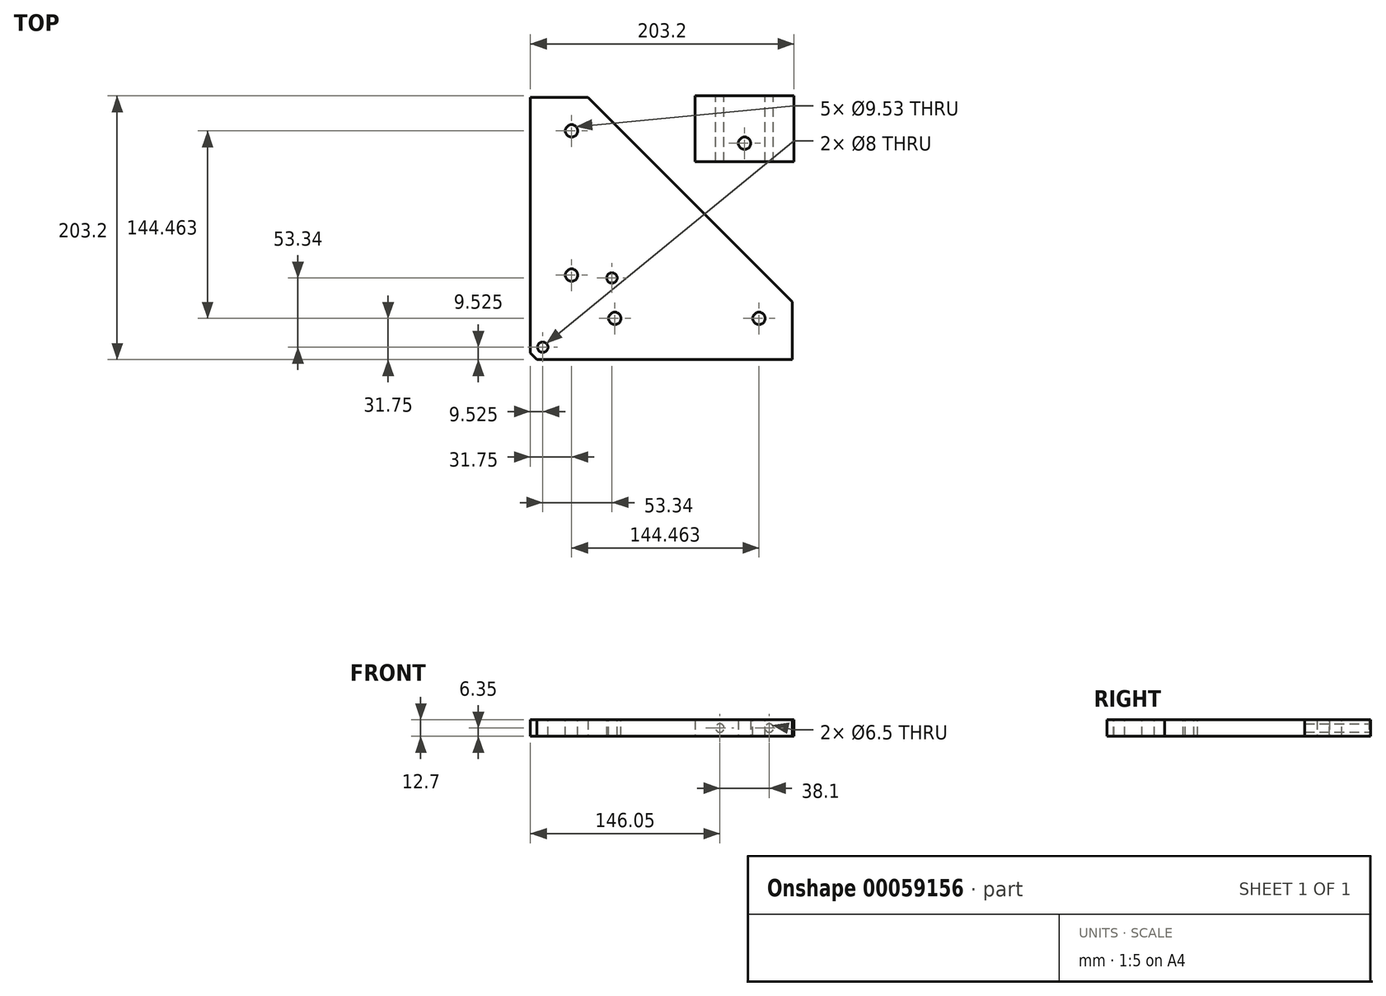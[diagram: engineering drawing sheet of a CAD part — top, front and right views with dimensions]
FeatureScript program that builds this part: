
annotation { "Feature Type Name" : "Feature", "Feature Type Description" : "" }
export const myFeature = defineFeature(function(context is Context, id is Id, definition is map)
    precondition{}
    {
        {
            var Q0;
            Q0=qCreatedBy(makeId("Top.planeOp"),FACE);
            var sketch = newSketch(context, id + "F0", { "sketchPlane" : qUnion([Q0])});
            skLineSegment(sketch, "E0", {"start": v(0, 0) * mm, "end": v(201.93, 0) * mm});
            skLineSegment(sketch, "E1", {"start": v(201.93, 0) * mm, "end": v(201.93, 44.45) * mm});
            skLineSegment(sketch, "E2", {"start": v(201.93, 44.45) * mm, "end": v(44.45, 201.93) * mm});
            skLineSegment(sketch, "E3", {"start": v(44.45, 201.93) * mm, "end": v(0, 201.93) * mm});
            skLineSegment(sketch, "E4", {"start": v(0, 201.93) * mm, "end": v(0, 0) * mm});
            skSolve(sketch);
        }
        {
            var Q0;
            Q0 = qSketchRegion(id + "F0", true);
            extrude(context, id + "F1", {"entities" : qUnion([Q0]), "depth" : 12.7 * mm});
        }
        {
            var Q0;
            Q0=makeQuery(id+"F1.opExtrude","CAP_FACE",FACE,{"disambiguationData":[OSD([sQuery(id+"F0.wireOp",EDGE,"E0"),sQuery(id+"F0.wireOp",EDGE,"E1"),sQuery(id+"F0.wireOp",EDGE,"E2"),sQuery(id+"F0.wireOp",EDGE,"E3"),sQuery(id+"F0.wireOp",EDGE,"E4")])],"isStart":false});
            var sketch = newSketch(context, id + "F2", { "sketchPlane" : qUnion([Q0])});
            skLineSegment(sketch, "E5", {"start": v(201.93, 31.75) * mm, "end": v(44.45, 31.75) * mm, "construction": true});
            skPoint(sketch, "E6", {"position": v(44.45, 31.75) * mm});
            skPoint(sketch, "E7.1.0.0", {"position": v(63.5, 31.75) * mm});
            skPoint(sketch, "E7.2.0.0", {"position": v(82.55, 31.75) * mm});
            skPoint(sketch, "E7.3.0.0", {"position": v(101.6, 31.75) * mm});
            skPoint(sketch, "E7.4.0.0", {"position": v(120.65, 31.75) * mm});
            skPoint(sketch, "E7.5.0.0", {"position": v(139.7, 31.75) * mm});
            skPoint(sketch, "E7.6.0.0", {"position": v(158.75, 31.75) * mm});
            skPoint(sketch, "E7.7.0.0", {"position": v(177.8, 31.75) * mm});
            skLineSegment(sketch, "E7.direction1", {"start": v(44.45, 31.75) * mm, "end": v(63.5, 31.75) * mm, "construction": true});
            skCircle(sketch, "E8", {"center": v(65.09, 31.75) * mm, "radius": 4.76 * mm});
            skCircle(sketch, "E9", {"center": v(176.21, 31.75) * mm, "radius": 4.76 * mm});
            skLineSegment(sketch, "E10", {"start": v(0, 0) * mm, "end": v(171.64, 171.64) * mm, "construction": true});
            skCircle(sketch, "E11.MirrorC", {"center": v(31.75, 176.21) * mm, "radius": 4.76 * mm});
            skCircle(sketch, "E12.MirrorC", {"center": v(31.75, 65.09) * mm, "radius": 4.76 * mm});
            skCircle(sketch, "E13", {"center": v(9.52, 9.53) * mm, "radius": 4 * mm});
            skCircle(sketch, "E14", {"center": v(62.87, 62.87) * mm, "radius": 4 * mm});
            skSolve(sketch);
        }
        {
            var Q0;
            Q0 = qSketchRegion(id + "F2", true);
            extrude(context, id + "F3", {"entities" : qUnion([Q0]), "operationType" : NewBodyOperationType.REMOVE, "endBound" : BoundingType.THROUGH_ALL, "oppositeDirection" : true, "depth" : 25.4 * mm});
        }
        {
            var Q0;
            Q0=makeQuery(id+"F1.opExtrude","SWEPT_EDGE",EDGE,{"disambiguationData":[OSD([sQuery(id+"F0.wireOp",EDGE,"E0"),sQuery(id+"F0.wireOp",EDGE,"E4")])]});
            chamfer(context, id + "F4", {"entities" : qUnion([Q0]), "width" : 5.08 * mm, "tangentPropagation" : true});
        }
        {
            var Q0;
            Q0=qCreatedBy(makeId("Top.planeOp"),FACE);
            var sketch = newSketch(context, id + "F5", { "sketchPlane" : qUnion([Q0])});
            skLineSegment(sketch, "E15.bottom", {"start": v(0, 0) * mm, "end": v(203.2, 0) * mm});
            skLineSegment(sketch, "E15.top", {"start": v(0, 203.2) * mm, "end": v(203.2, 203.2) * mm});
            skLineSegment(sketch, "E15.left", {"start": v(0, 0) * mm, "end": v(0, 203.2) * mm});
            skLineSegment(sketch, "E15.right", {"start": v(203.2, 0) * mm, "end": v(203.2, 203.2) * mm});
            skSolve(sketch);
        }
        {
            var Q0;
            Q0=qCreatedBy(makeId("Top.planeOp"),FACE);
            var sketch = newSketch(context, id + "F6", { "sketchPlane" : qUnion([Q0])});
            skLineSegment(sketch, "E16", {"start": v(127, 203.2) * mm, "end": v(203.2, 203.2) * mm});
            skLineSegment(sketch, "E17", {"start": v(203.2, 203.2) * mm, "end": v(203.2, 127) * mm});
            skLineSegment(sketch, "E18", {"start": v(203.2, 127) * mm, "end": v(190.5, 127) * mm});
            skLineSegment(sketch, "E19", {"start": v(190.5, 127) * mm, "end": v(190.5, 177.8) * mm});
            skLineSegment(sketch, "E20", {"start": v(127, 203.2) * mm, "end": v(127, 190.5) * mm});
            skLineSegment(sketch, "E21", {"start": v(127, 190.5) * mm, "end": v(177.8, 190.5) * mm});
            skArc(sketch, "E22", {"start": v(177.8, 190.5) * mm, "mid": v(186.78, 186.78) * mm, "end": v(190.5, 177.8) * mm});
            skSolve(sketch);
        }
        {
            var Q0;
            Q0 = qSketchRegion(id + "F6", true);
            extrude(context, id + "F7", {"entities" : qUnion([Q0]), "depth" : 12.7 * mm});
        }
        {
            var Q0;
            Q0=makeQuery(id+"F7.opExtrude","SWEPT_FACE",FACE,{"disambiguationData":[OSD([sQuery(id+"F6.wireOp",EDGE,"E17")])]});
            var sketch = newSketch(context, id + "F8", { "sketchPlane" : qUnion([Q0])});
            skCircle(sketch, "E23", {"center": v(185, 6.35) * mm, "radius": 4 * mm});
            skLineSegment(sketch, "E24", {"start": v(185, 0) * mm, "end": v(185, 12.7) * mm, "construction": true});
            skCircle(sketch, "E25", {"center": v(166.67, 6.35) * mm, "radius": 4 * mm});
            skSolve(sketch);
        }
        {
            var Q0;
            Q0 = qSketchRegion(id + "F8", true);
            extrude(context, id + "F9", {"entities" : qUnion([Q0]), "operationType" : NewBodyOperationType.REMOVE, "endBound" : BoundingType.UP_TO_NEXT, "oppositeDirection" : true, "depth" : 25.4 * mm});
        }
        {
            var Q0;
            Q0=makeQuery(id+"F7.opExtrude","SWEPT_BODY",BODY,{"disambiguationData":[OSD([sQuery(id+"F6.wireOp",EDGE,"E16"),sQuery(id+"F6.wireOp",EDGE,"E17"),sQuery(id+"F6.wireOp",EDGE,"E18"),sQuery(id+"F6.wireOp",EDGE,"E19"),sQuery(id+"F6.wireOp",EDGE,"E20"),sQuery(id+"F6.wireOp",EDGE,"E21"),sQuery(id+"F6.wireOp",EDGE,"E22")])]});
            deleteBodies(context, id + "F10", {"entities" : qUnion([Q0])});
        }
        {
            var Q0;
            Q0=makeQuery(id+"F5.imprint","IMPRINT",FACE,{"disambiguationData":[TD([[makeQuery(id+"F5.imprint","IMPRINT",EDGE,{"derivedFrom":sQuery(id+"F5.wireOp",EDGE,"E15.bottom")}),1.0]])]});
            var sketch = newSketch(context, id + "F11", { "sketchPlane" : qUnion([Q0])});
            skLineSegment(sketch, "E26.bottom", {"start": v(127, 203.2) * mm, "end": v(203.2, 203.2) * mm});
            skLineSegment(sketch, "E26.top", {"start": v(127, 152.4) * mm, "end": v(203.2, 152.4) * mm});
            skLineSegment(sketch, "E26.left", {"start": v(127, 203.2) * mm, "end": v(127, 152.4) * mm});
            skLineSegment(sketch, "E26.right", {"start": v(203.2, 203.2) * mm, "end": v(203.2, 152.4) * mm});
            skCircle(sketch, "E27", {"center": v(165.1, 166.67) * mm, "radius": 4.76 * mm});
            skPoint(sketch, "E27.centerSnap0", {"position": v(165.1, 203.2) * mm});
            skSolve(sketch);
        }
        {
            var Q0;
            Q0 = qSketchRegion(id + "F11", true);
            extrude(context, id + "F12", {"entities" : qUnion([Q0]), "depth" : 12.7 * mm});
        }
        {
            var Q0;
            Q0=makeQuery(id+"F12.opExtrude","SWEPT_FACE",FACE,{"disambiguationData":[OSD([sQuery(id+"F11.wireOp",EDGE,"E26.bottom")])]});
            var sketch = newSketch(context, id + "F13", { "sketchPlane" : qUnion([Q0])});
            skCircle(sketch, "E28", {"center": v(-184.15, 6.35) * mm, "radius": 3.25 * mm});
            skPoint(sketch, "E28.centerSnap0", {"position": v(-203.2, 6.35) * mm});
            skCircle(sketch, "E29", {"center": v(-146.05, 6.35) * mm, "radius": 3.25 * mm});
            skSolve(sketch);
        }
        {
            var Q0;
            Q0=makeQuery(id+"F13.imprint","IMPRINT",FACE,{"disambiguationData":[TD([[makeQuery(id+"F13.imprint","IMPRINT",EDGE,{"derivedFrom":sQuery(id+"F13.wireOp",EDGE,"E28")}),1.0]])]});
            var Q1;
            Q1=makeQuery(id+"F13.imprint","IMPRINT",FACE,{"disambiguationData":[TD([[makeQuery(id+"F13.imprint","IMPRINT",EDGE,{"derivedFrom":sQuery(id+"F13.wireOp",EDGE,"E29")}),1.0]])]});
            extrude(context, id + "F14", {"entities" : qUnion([Q0, Q1]), "operationType" : NewBodyOperationType.REMOVE, "endBound" : BoundingType.UP_TO_NEXT, "oppositeDirection" : true, "depth" : 25.4 * mm});
        }
    });
